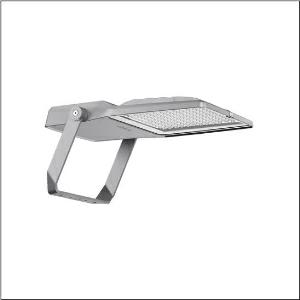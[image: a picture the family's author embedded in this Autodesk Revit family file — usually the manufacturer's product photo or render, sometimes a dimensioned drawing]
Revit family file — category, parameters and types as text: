
# Revit family: floodlight_fl_21_iq_midi___rs12_5xa7782f3b1a_f18b
name_source: partatom
category: Lighting Fixtures
units: mm (PartAtom-declared; Revit-internal decimal feet)

## family parameters
Cut with Voids When Loaded = No
Host = Face
Light Source = No
Part Type = Normal
Room Calculation Point = No
Round Connector Dimension = Use Diameter
Shared = No

## types (1)
- --- (1 x LED, 30610 lm, 270.2 W, 3000K)
    Apparent Load = 270 VA
    CIE Flux Codes = 79 92 99 100 100
    Color Rendering = 80
    Color Temperature = 3000K
    Default Elevation = 1800 mm
    Description = Floodlight FL 21 iQ midi, floodlight, primary light control with lens, of PMMA, primary optical cover: protective disc, of toughened safety glass, transparent, light distribution: RS12, light emission: direct distribution, installation type: surface-mounted, LED, High Power LED, rated luminous flux: 30.610lm, luminous efficacy: 113lm/W, light colour: 830, colour temperature: 3000K, control gear: ECG iQ, control: optimised constant luminous flux control (CLO 2.0), Desk-Remote (wireless, voltage-free reading and setting of iQ features in the workshop via application-optimized NFC function/RFID function), Smart-Wire, Night-Set, Temp-Guard, Street-Remote, Auto-Match, with terminal, 6-pole, mains connection: 220..240V, AC, 50/60Hz, start of lifetime: 270W, end of service life: 287W, reduction: 117W, luminaire housing, of diecast aluminium, powder-coated, Siteco® metallic grey (DB 702S), corrosivity category C5 mid according to DIN EN ISO 12944, sealing non-destructively replaceable, mounting bracket, of steel, galvanised, powder-coated, Siteco® metallic grey (DB 702S), protection rating (complete): IP66, insulation class (complete): insulation class II (safety insulation), certification: CE, protection symbol: D, impact resistance: IK08, permissible operating ambient temperature: -40..+40°C, permissible operating ambient temperature for outdoor applications: -40..+50°C, standard: DIN EN 12944, LABS conformity tested according to VDMA 24364:2018-05, packaging unit: 1 piece

Light Distribution: RS12
    Height = 76 mm
    Lamp = 1 x LED
    Lamp Light Flux = 30610 lm
    Lamp Power = 270.2 W
    Lamp count = 1
    Length = 657 mm
    Luminous efficacy = 113 lm/W
    Manufacturer = Siteco
    ModVariant = No
    Model = 5XA7782F3B1A
    Number of Poles = 1
    OnlyDefault = Yes
    Power Factor = 1
    Product Name = Floodlight FL 21 iQ midi | RS12
    Product group = floodlight | pylon annexe
    ProductGroupID = 6200
    Protection Class = Protection class II
    Protection Degree = IP 66
    RLX_Detail_Level = 1
    RLX_Emergency_Light_Flux = 0 lm
    RLX_Emergency_Type = 0
    RLX_Emergency_Type_DB = No
    RlxData = <blob elided: 141013 chars, md5=07052d20>
    Socket = socket
    Standby Power = 0 W
    System Light Flux = 30610 lm
    System Power = 270 W
    Type Comments = factory setting: luminous flux: 100 % | dim-lin: 254 | 620 mA
    Type Image = l_1006876.jpg
    URL = http://relux.com
    VarID = @adj_037603
    Voltage = 0 V
    Weight = 0.00 kg
    Width = 442 mm

## geometry (parser evidence)
native form markers: Blend x4, Sweep x11
no freeform markers — native parametric forms only
